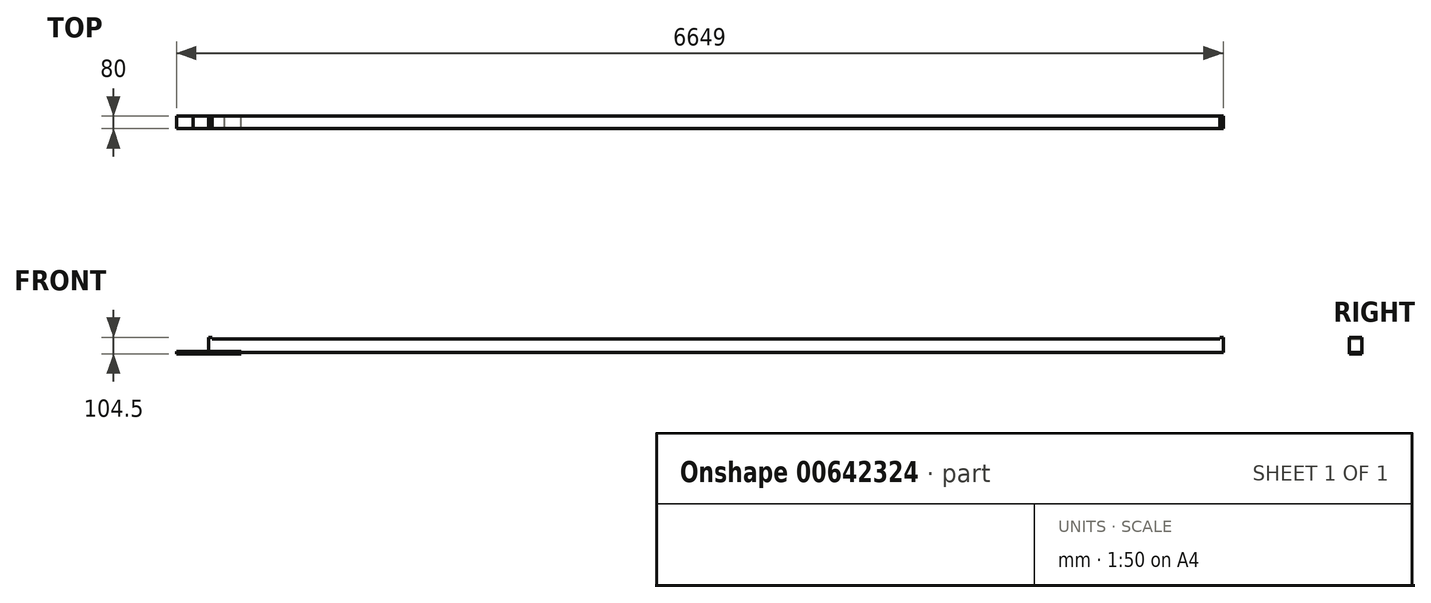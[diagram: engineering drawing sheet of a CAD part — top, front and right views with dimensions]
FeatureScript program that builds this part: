
annotation { "Feature Type Name" : "Feature", "Feature Type Description" : "" }
export const myFeature = defineFeature(function(context is Context, id is Id, definition is map)
    precondition{}
    {
        {
            var Q0;
            Q0=qCreatedBy(makeId("Front.planeOp"),FACE);
            var sketch = newSketch(context, id + "F0", { "sketchPlane" : qUnion([Q0])});
            skLineSegment(sketch, "E0", {"start": v(0, 97) * mm, "end": v(0, 0) * mm});
            skLineSegment(sketch, "E1", {"start": v(0, 0) * mm, "end": v(6444, 0) * mm});
            skLineSegment(sketch, "E2", {"start": v(6444, 0) * mm, "end": v(6444, 97) * mm});
            skLineSegment(sketch, "E3", {"start": v(6444, 97) * mm, "end": v(6422, 97) * mm});
            skLineSegment(sketch, "E4", {"start": v(6422, 97) * mm, "end": v(6422, 85) * mm});
            skLineSegment(sketch, "E5", {"start": v(6422, 85) * mm, "end": v(22, 85) * mm});
            skLineSegment(sketch, "E6", {"start": v(22, 85) * mm, "end": v(22, 97) * mm});
            skLineSegment(sketch, "E7", {"start": v(22, 97) * mm, "end": v(0, 97) * mm});
            skSolve(sketch);
        }
        {
            var Q0;
            Q0=makeQuery(id+"F0.imprint","IMPRINT",FACE,{"disambiguationData":[TD([[makeQuery(id+"F0.imprint","IMPRINT",EDGE,{"derivedFrom":sQuery(id+"F0.wireOp",EDGE,"E0")}),1.0]])]});
            extrude(context, id + "F1", {"entities" : qUnion([Q0]), "depth" : 80 * mm, "offsetDistance" : 25 * mm});
        }
        {
            var Q0;
            Q0=qCreatedBy(makeId("Front.planeOp"),FACE);
            var sketch = newSketch(context, id + "F2", { "sketchPlane" : qUnion([Q0])});
            skLineSegment(sketch, "E8.bottom", {"start": v(205, -7.5) * mm, "end": v(-205, -7.5) * mm});
            skLineSegment(sketch, "E8.top", {"start": v(205, 7.5) * mm, "end": v(-205, 7.5) * mm});
            skLineSegment(sketch, "E8.left", {"start": v(205, -7.5) * mm, "end": v(205, 7.5) * mm});
            skLineSegment(sketch, "E8.right", {"start": v(-205, -7.5) * mm, "end": v(-205, 7.5) * mm});
            skPoint(sketch, "E8.middle", {"position": v(0, 0) * mm});
            skSolve(sketch);
        }
        {
            var Q0;
            Q0=makeQuery(id+"F2.imprint","IMPRINT",FACE,{"disambiguationData":[TD([[makeQuery(id+"F2.imprint","IMPRINT",EDGE,{"derivedFrom":sQuery(id+"F2.wireOp",EDGE,"E8.bottom")}),-1.0]])]});
            extrude(context, id + "F3", {"entities" : qUnion([Q0]), "depth" : 80 * mm, "offsetDistance" : 25 * mm});
        }
        {
            var Q0;
            Q0=qCreatedBy(makeId("Front.planeOp"),FACE);
            var sketch = newSketch(context, id + "F4", { "sketchPlane" : qUnion([Q0])});
            skLineSegment(sketch, "E9.bottom", {"start": v(100, -7.5) * mm, "end": v(-100, -7.5) * mm});
            skLineSegment(sketch, "E9.top", {"start": v(100, 7.5) * mm, "end": v(-100, 7.5) * mm});
            skLineSegment(sketch, "E9.left", {"start": v(100, -7.5) * mm, "end": v(100, 7.5) * mm});
            skLineSegment(sketch, "E9.right", {"start": v(-100, -7.5) * mm, "end": v(-100, 7.5) * mm});
            skPoint(sketch, "E9.middle", {"position": v(0, 0) * mm});
            skSolve(sketch);
        }
        {
            var Q0;
            Q0=makeQuery(id+"F4.imprint","IMPRINT",FACE,{"disambiguationData":[TD([[makeQuery(id+"F4.imprint","IMPRINT",EDGE,{"derivedFrom":sQuery(id+"F4.wireOp",EDGE,"E9.bottom")}),-1.0]])]});
            extrude(context, id + "F5", {"entities" : qUnion([Q0]), "depth" : 80 * mm, "offsetDistance" : 25 * mm});
        }
    });
